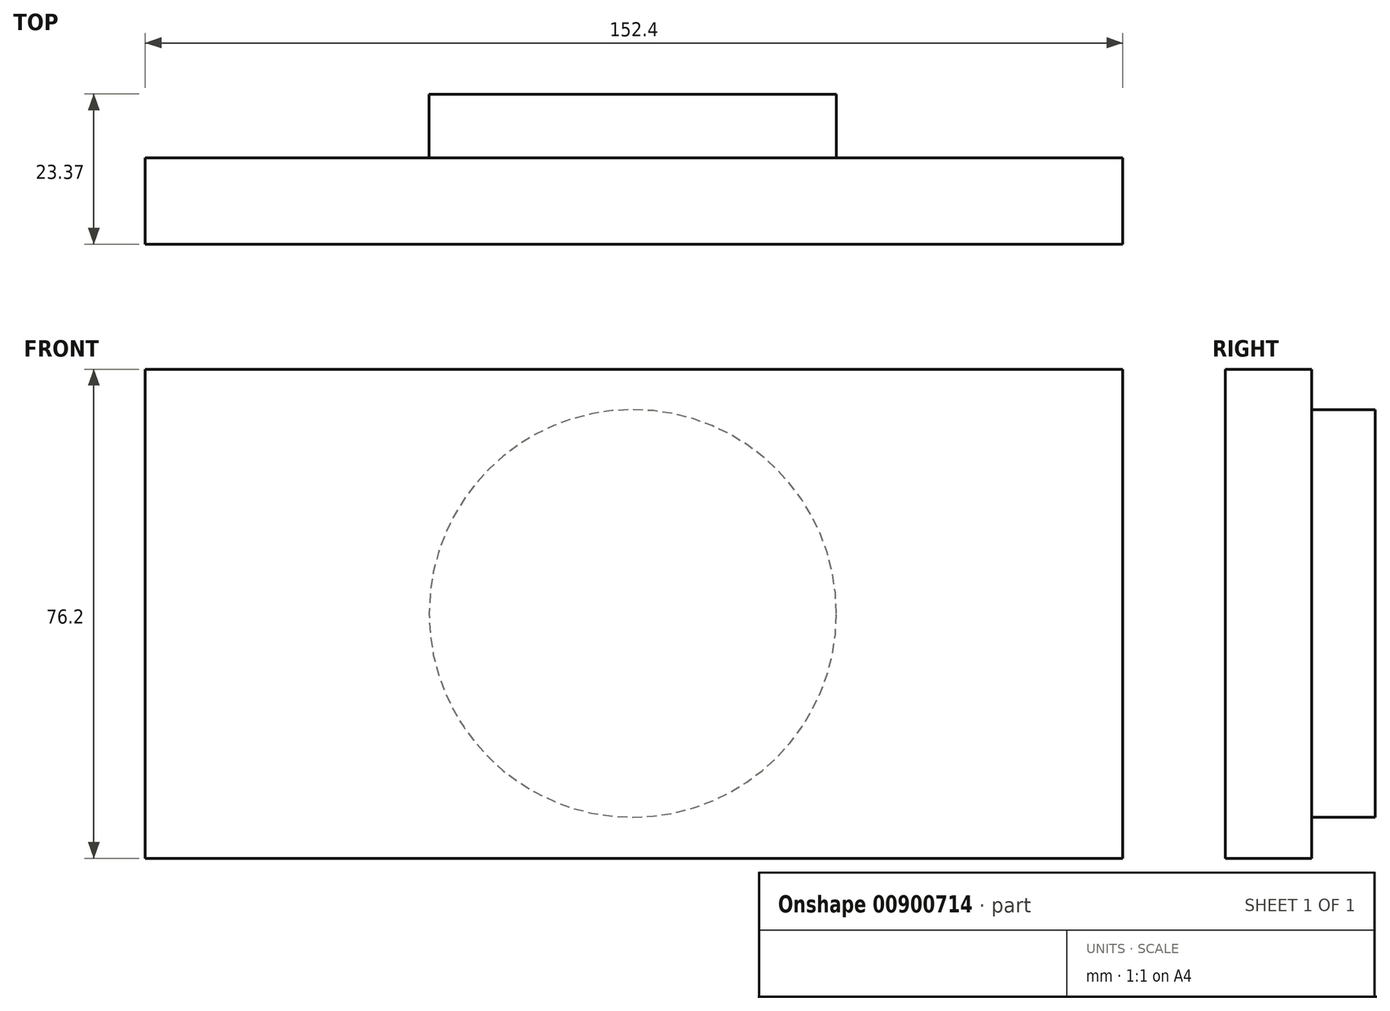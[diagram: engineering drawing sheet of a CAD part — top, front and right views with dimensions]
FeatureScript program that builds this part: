
annotation { "Feature Type Name" : "Feature", "Feature Type Description" : "" }
export const myFeature = defineFeature(function(context is Context, id is Id, definition is map)
    precondition{}
    {
        {
            var Q0;
            Q0=qCreatedBy(makeId("Front.planeOp"),FACE);
            var sketch = newSketch(context, id + "F0", { "sketchPlane" : qUnion([Q0])});
            skLineSegment(sketch, "E0.bottom", {"start": v(-76, 38.05) * mm, "end": v(76.4, 38.05) * mm});
            skLineSegment(sketch, "E0.top", {"start": v(-76, -38.15) * mm, "end": v(76.4, -38.15) * mm});
            skLineSegment(sketch, "E0.left", {"start": v(-76, 38.05) * mm, "end": v(-76, -38.15) * mm});
            skLineSegment(sketch, "E0.right", {"start": v(76.4, 38.05) * mm, "end": v(76.4, -38.15) * mm});
            skLineSegment(sketch, "E1", {"start": v(-76, 38.05) * mm, "end": v(76.4, -38.15) * mm});
            skLineSegment(sketch, "E2", {"start": v(76.4, 38.05) * mm, "end": v(-76, -38.15) * mm});
            skSolve(sketch);
        }
        {
            var Q0;
            Q0 = qSketchRegion(id + "F0", true);
            extrude(context, id + "F1", {"entities" : qUnion([Q0]), "depth" : 13.46 * mm, "offsetDistance" : 25.4 * mm});
        }
        {
            var Q0;
            Q0=qCreatedBy(makeId("Front.planeOp"),FACE);
            var sketch = newSketch(context, id + "F2", { "sketchPlane" : qUnion([Q0])});
            skCircle(sketch, "E3", {"center": v(0, 0) * mm, "radius": 31.75 * mm});
            skSolve(sketch);
        }
        {
            var Q0;
            Q0 = qSketchRegion(id + "F2", true);
            extrude(context, id + "F3", {"entities" : qUnion([Q0]), "operationType" : NewBodyOperationType.ADD, "oppositeDirection" : true, "depth" : 9.9 * mm, "offsetDistance" : 25.4 * mm});
        }
    });
